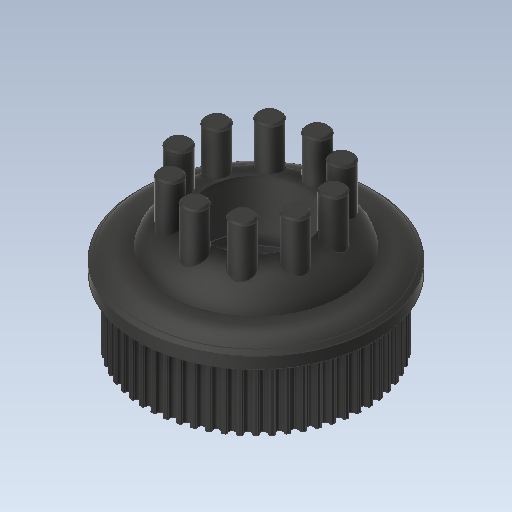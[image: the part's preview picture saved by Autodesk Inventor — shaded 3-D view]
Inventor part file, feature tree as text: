
AUTODESK INVENTOR PART (.ipt)
format: ipt  version: 2020.1 (Build 241239000, 239)  size: 993,280 bytes
history: native  units: mm
features: sketch x6, extrude x5, chamfer x4, fillet x3, other x1, pattern_circular x1, plane x1
ambient origin geometry x8: Origin, YZ Plane, XZ Plane, XY Plane, X Axis, Y Axis, Z Axis, Center Point
bodies: Solid1 (feature_tree)
feature tree (21):
  other  "gates_P60-3M-09AL.ipt"
  extrude  "Extrusion1"  Depth=7.0mm
  fillet  "Fillet1"  Radius=7.0mm
  extrude  "Extrusion2"  Depth=10.0mm
  chamfer  "Chamfer1"  Distance=18.0mm
  pattern_circular  "Circular Pattern1"  Count=10 Angle=360.0deg
  plane  "Work Plane1"
  sketch  "Sketch3"  dims[d9=0.5mm d10=2.0mm d11=45.0deg d12=100.0mm d13=360.0deg]
  extrude  "Extrusion3"  Depth=0.938mm
  chamfer  "Chamfer2"  Distance=2.4mm
  extrude  "Extrusion8"  Depth=7.0mm TaperAngle=0.0deg
  extrude  "Extrusion9"  Depth=7.0mm TaperAngle=45.0deg
  chamfer  "Chamfer5"  Distance=1.2mm
  fillet  "Fillet4"  Radius=10.0mm
  chamfer  "Chamfer6"  Distance=56.54mm
  fillet  "Fillet5"  Radius=11.0mm
  sketch  "Sketch1"  dims[d0=44.8mm d1=25.0mm d2=7.0mm d3=0.0mm]
  sketch  "Sketch2"  dims[d6=15.85mm d7=18.0mm d8=0.0mm]
  sketch  "Sketch4"  dims[d15=20.0mm d16=0.938mm]
  sketch  "Sketch2_1"  dims[d4=10.0mm d5=5.8mm]
  sketch  "Sketch11"  dims[d17=23.873241mm d18=2.4mm d19=7.0mm d20=0.0mm d24=2.4mm d25=1.0mm d26=45.0deg d50=1.2mm d52=10.0mm d53=56.54mm d54=11.0mm d55=0.0mm d56=10.0mm d57=0.0mm d60=3.0mm d61=2.0mm d62=45.0deg d63=7.0mm d71=9.5mm d72=14.65mm d73=45.0deg d74=7.0mm d75=5.0mm d76=0.0mm]
